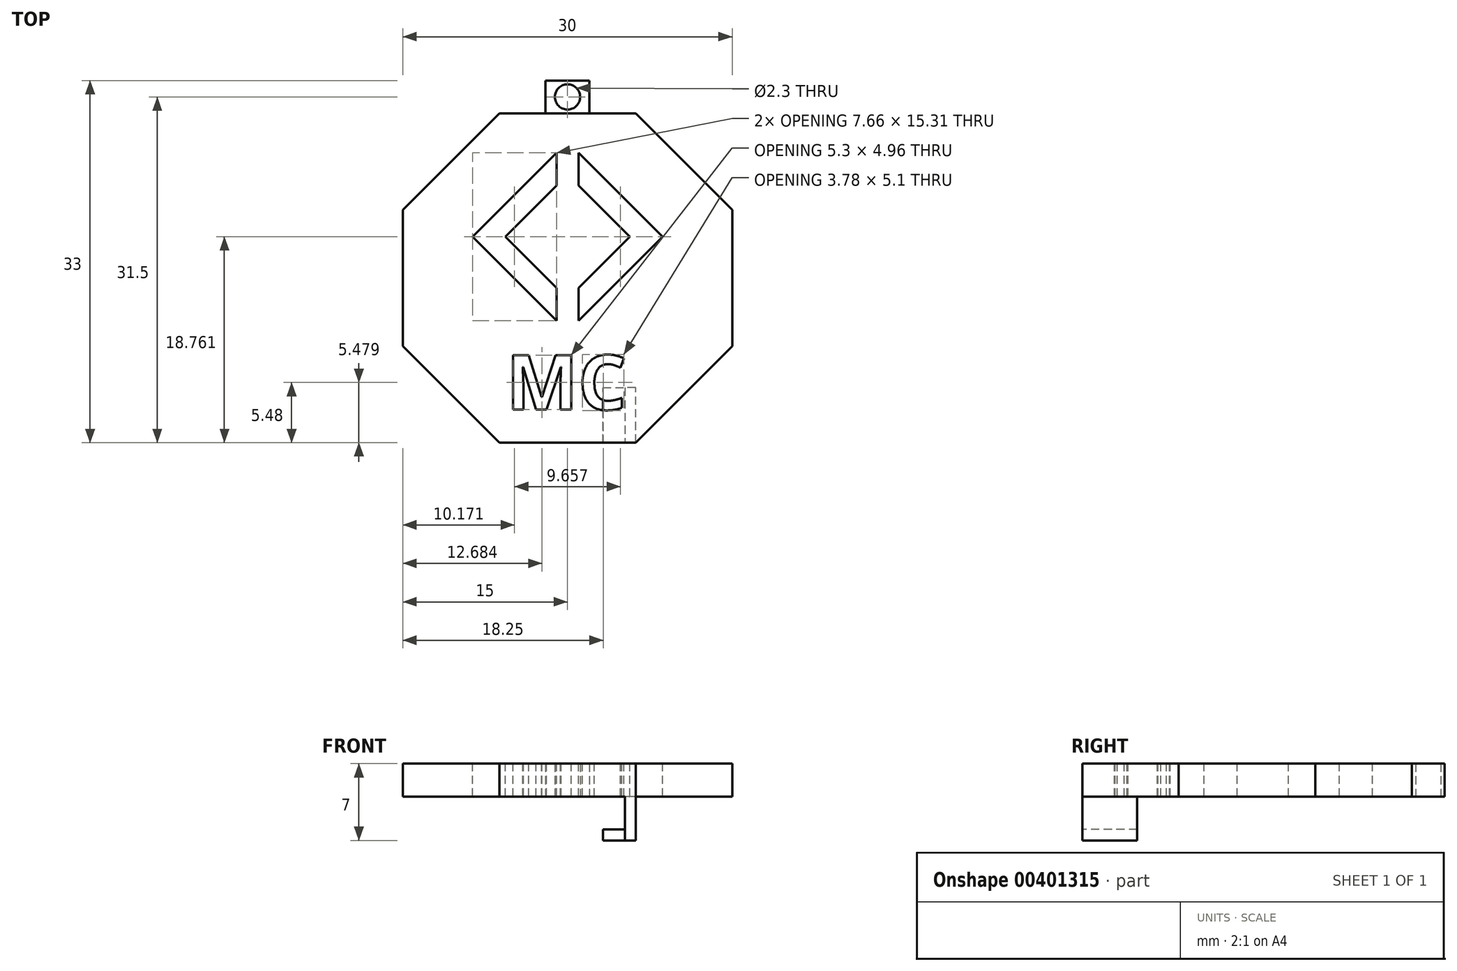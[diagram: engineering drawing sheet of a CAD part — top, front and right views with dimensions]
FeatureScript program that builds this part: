
annotation { "Feature Type Name" : "Feature", "Feature Type Description" : "" }
export const myFeature = defineFeature(function(context is Context, id is Id, definition is map)
    precondition{}
    {
        {
            var Q0;
            Q0=qCreatedBy(makeId("Top.planeOp"),FACE);
            var sketch = newSketch(context, id + "F0", { "sketchPlane" : qUnion([Q0])});
            skCircle(sketch, "E0.cCircle", {"center": v(0, 0) * mm, "radius": 15 * mm, "construction": true});
            skLineSegment(sketch, "E0.0", {"start": v(15, 6.21) * mm, "end": v(15, -6.21) * mm});
            skLineSegment(sketch, "E0.1", {"start": v(15, -6.21) * mm, "end": v(6.21, -15) * mm});
            skLineSegment(sketch, "E0.2", {"start": v(6.21, -15) * mm, "end": v(-6.21, -15) * mm});
            skLineSegment(sketch, "E0.3", {"start": v(-6.21, -15) * mm, "end": v(-15, -6.21) * mm});
            skLineSegment(sketch, "E0.4", {"start": v(-15, -6.21) * mm, "end": v(-15, 6.21) * mm});
            skLineSegment(sketch, "E0.5", {"start": v(-15, 6.21) * mm, "end": v(-6.21, 15) * mm});
            skLineSegment(sketch, "E0.6", {"start": v(-6.21, 15) * mm, "end": v(6.21, 15) * mm});
            skLineSegment(sketch, "E0.7", {"start": v(6.21, 15) * mm, "end": v(15, 6.21) * mm});
            skPoint(sketch, "E0.0.midPoint", {"position": v(15, 0) * mm});
            skLineSegment(sketch, "E1", {"start": v(0, 0) * mm, "end": v(-15, 0) * mm, "construction": true});
            skSolve(sketch);
        }
        {
            var Q0;
            Q0=qSketchRegion(id+"F0",true);
            extrude(context, id + "F1", {"entities" : qUnion([Q0]), "depth" : 3 * mm});
        }
        {
            var Q0;
            Q0=makeQuery(id+"F1.opExtrude","CAP_FACE",FACE,{"disambiguationData":[OSD([sQuery(id+"F0.wireOp",EDGE,"E0.0"),sQuery(id+"F0.wireOp",EDGE,"E0.1"),sQuery(id+"F0.wireOp",EDGE,"E0.2"),sQuery(id+"F0.wireOp",EDGE,"E0.3"),sQuery(id+"F0.wireOp",EDGE,"E0.4"),sQuery(id+"F0.wireOp",EDGE,"E0.5"),sQuery(id+"F0.wireOp",EDGE,"E0.6"),sQuery(id+"F0.wireOp",EDGE,"E0.7")])],"isStart":false});
            var sketch = newSketch(context, id + "F2", { "sketchPlane" : qUnion([Q0])});
            skText(sketch, "E2", { "text": "MC", "fontName": "OpenSans-Bold.ttf"});
            skArc(sketch, "E3.cCircle", {"start": v(2.83, 0.93) * mm, "mid": v(0, 7.76) * mm, "end": v(-2.83, 0.93) * mm, "construction": true});
            skLineSegment(sketch, "E3.0", {"start": v(5.66, 3.76) * mm, "end": v(1, -0.9) * mm});
            skLineSegment(sketch, "E3.2", {"start": v(-5.66, 3.76) * mm, "end": v(-1, 8.42) * mm});
            skLineSegment(sketch, "E3.3", {"start": v(1, 8.42) * mm, "end": v(5.66, 3.76) * mm});
            skPoint(sketch, "E3.0.midPoint", {"position": v(2.83, 0.93) * mm});
            skLineSegment(sketch, "E4", {"start": v(-5.66, 3.76) * mm, "end": v(0, 3.76) * mm, "construction": true});
            skLineSegment(sketch, "E5.1", {"start": v(8.66, 3.76) * mm, "end": v(1, -3.9) * mm});
            skLineSegment(sketch, "E5.3", {"start": v(-8.66, 3.76) * mm, "end": v(-1, 11.42) * mm});
            skPoint(sketch, "E5.0.midPoint", {"position": v(4.33, 8.1) * mm});
            skLineSegment(sketch, "E6", {"start": v(-8.66, 3.76) * mm, "end": v(-5.66, 3.76) * mm, "construction": true});
            skPoint(sketch, "E7.orphan", {"position": v(0, -1.9) * mm});
            skPoint(sketch, "E8.orphan", {"position": v(0, -4.9) * mm});
            skPoint(sketch, "E9.orphan", {"position": v(0.45, -660.17) * mm});
            skPoint(sketch, "E10.orphan", {"position": v(-0.45, -23.95) * mm});
            skLineSegment(sketch, "E11.trimOffspring", {"start": v(0, 3.76) * mm, "end": v(8.66, 3.76) * mm, "construction": true});
            skPoint(sketch, "E12.orphan", {"position": v(0, 9.42) * mm});
            skPoint(sketch, "E13.orphan", {"position": v(0, 12.42) * mm});
            skPoint(sketch, "E14.bottom.end.orphan", {"position": v(0.45, 31.48) * mm});
            skPoint(sketch, "E14.bottom.start.orphan", {"position": v(-0.45, 667.69) * mm});
            skPoint(sketch, "E15.firstSnap0", {"position": v(-10.6, -10.6) * mm});
            skPoint(sketch, "E15.secondSnap0", {"position": v(10.6, 10.6) * mm});
            skPoint(sketch, "E16.startSnap0", {"position": v(0.45, 11.37) * mm});
            skLineSegment(sketch, "E17", {"start": v(1, 11.42) * mm, "end": v(1, 8.42) * mm});
            skLineSegment(sketch, "E18", {"start": v(-1, 11.42) * mm, "end": v(-1, 8.42) * mm});
            skPoint(sketch, "E19.orphan", {"position": v(0.45, 12.87) * mm});
            skLineSegment(sketch, "E20.trimOffspring", {"start": v(1, 11.42) * mm, "end": v(8.66, 3.76) * mm});
            skPoint(sketch, "E21.trimOffspring.end.orphan", {"position": v(0.45, 9.87) * mm});
            skLineSegment(sketch, "E22.trimOffspring", {"start": v(-1, -0.9) * mm, "end": v(-5.66, 3.76) * mm});
            skLineSegment(sketch, "E23.trimOffspring", {"start": v(-1, -0.9) * mm, "end": v(-1, -3.9) * mm});
            skLineSegment(sketch, "E24.trimOffspring", {"start": v(1, -0.9) * mm, "end": v(1, -3.9) * mm});
            skLineSegment(sketch, "E25.trimOffspring", {"start": v(-1, -3.9) * mm, "end": v(-8.66, 3.76) * mm});
            const initialGuessF2  = {"E2": [-0.00559, -0.012, 1, 0, 0.005]};
            skSetInitialGuess(sketch, initialGuessF2);
            skSolve(sketch);
        }
        {
            var Q0;
            Q0=qSketchRegion(id+"F2",true);
            extrude(context, id + "F3", {"entities" : qUnion([Q0]), "operationType" : NewBodyOperationType.REMOVE, "endBound" : BoundingType.THROUGH_ALL, "oppositeDirection" : true, "depth" : 3 * mm});
        }
        {
            var Q0;
            Q0=makeQuery(id+"F1.opExtrude","CAP_FACE",FACE,{"disambiguationData":[OSD([sQuery(id+"F0.wireOp",EDGE,"E0.0"),sQuery(id+"F0.wireOp",EDGE,"E0.1"),sQuery(id+"F0.wireOp",EDGE,"E0.2"),sQuery(id+"F0.wireOp",EDGE,"E0.3"),sQuery(id+"F0.wireOp",EDGE,"E0.4"),sQuery(id+"F0.wireOp",EDGE,"E0.5"),sQuery(id+"F0.wireOp",EDGE,"E0.6"),sQuery(id+"F0.wireOp",EDGE,"E0.7")])],"isStart":true});
            var sketch = newSketch(context, id + "F4", { "sketchPlane" : qUnion([Q0])});
            skLineSegment(sketch, "E26.bottom", {"start": v(6.21, 15) * mm, "end": v(5.21, 15) * mm});
            skLineSegment(sketch, "E26.top", {"start": v(6.21, 10) * mm, "end": v(5.21, 10) * mm});
            skLineSegment(sketch, "E26.left", {"start": v(6.21, 15) * mm, "end": v(6.21, 10) * mm});
            skLineSegment(sketch, "E26.right", {"start": v(5.21, 15) * mm, "end": v(5.21, 10) * mm});
            skSolve(sketch);
        }
        {
            var Q0;
            Q0=qSketchRegion(id+"F4",true);
            extrude(context, id + "F5", {"entities" : qUnion([Q0]), "operationType" : NewBodyOperationType.ADD, "depth" : 4 * mm});
        }
        {
            var Q0;
            Q0=makeQuery(id+"F5.opExtrude","SWEPT_FACE",FACE,{"disambiguationData":[OSD([sQuery(id+"F4.wireOp",EDGE,"E26.right")])]});
            var sketch = newSketch(context, id + "F6", { "sketchPlane" : qUnion([Q0])});
            skLineSegment(sketch, "E27.bottom", {"start": v(10, -4) * mm, "end": v(15, -4) * mm});
            skLineSegment(sketch, "E27.top", {"start": v(10, -3) * mm, "end": v(15, -3) * mm});
            skLineSegment(sketch, "E27.left", {"start": v(10, -4) * mm, "end": v(10, -3) * mm});
            skLineSegment(sketch, "E27.right", {"start": v(15, -4) * mm, "end": v(15, -3) * mm});
            skSolve(sketch);
        }
        {
            var Q0;
            Q0=makeQuery(id+"F6.imprint","IMPRINT",FACE,{"disambiguationData":[TD([[makeQuery(id+"F6.imprint","IMPRINT",EDGE,{"derivedFrom":sQuery(id+"F6.wireOp",EDGE,"E27.bottom")}),-1.0]])]});
            var Q1;
            Q1=sQuery(id+"F6.wireOp",EDGE,"E27.top");
            var Q2;
            Q2=sQuery(id+"F6.wireOp",EDGE,"E27.bottom");
            var Q3;
            Q3=sQuery(id+"F6.wireOp",EDGE,"E27.right");
            var Q4;
            Q4=sQuery(id+"F6.wireOp",EDGE,"E27.left");
            extrude(context, id + "F7", {"entities" : qUnion([Q0]), "surfaceEntities" : qUnion([Q1, Q2, Q3, Q4]), "depth" : 2 * mm});
        }
        {
            var Q0;
            Q0=makeQuery(id+"F1.opExtrude","SWEPT_FACE",FACE,{"disambiguationData":[OSD([sQuery(id+"F0.wireOp",EDGE,"E0.6")])]});
            var sketch = newSketch(context, id + "F8", { "sketchPlane" : qUnion([Q0])});
            skLineSegment(sketch, "E28.bottom", {"start": v(2, 3) * mm, "end": v(-2, 3) * mm});
            skLineSegment(sketch, "E28.top", {"start": v(2, 0) * mm, "end": v(-2, 0) * mm});
            skLineSegment(sketch, "E28.left", {"start": v(2, 3) * mm, "end": v(2, 0) * mm});
            skLineSegment(sketch, "E28.right", {"start": v(-2, 3) * mm, "end": v(-2, 0) * mm});
            skPoint(sketch, "E28.middle", {"position": v(0, 1.5) * mm});
            skPoint(sketch, "E28.middle.positionSnap0", {"position": v(0, 3) * mm});
            skPoint(sketch, "E28.centerSnap0", {"position": v(0, 3) * mm});
            skSolve(sketch);
        }
        {
            var Q0;
            Q0=qSketchRegion(id+"F8",true);
            extrude(context, id + "F9", {"entities" : qUnion([Q0]), "depth" : 3 * mm});
        }
        {
            var Q0;
            Q0=makeQuery(id+"F9.opExtrude","SWEPT_FACE",FACE,{"disambiguationData":[OSD([sQuery(id+"F8.wireOp",EDGE,"E28.top")])]});
            var sketch = newSketch(context, id + "F10", { "sketchPlane" : qUnion([Q0])});
            skCircle(sketch, "E29", {"center": v(0, -16.5) * mm, "radius": 1.15 * mm});
            skLineSegment(sketch, "E30", {"start": v(0, -16.5) * mm, "end": v(0, -15) * mm, "construction": true});
            skLineSegment(sketch, "E31", {"start": v(0, -16.5) * mm, "end": v(0, -18) * mm, "construction": true});
            skSolve(sketch);
        }
        {
            var Q0;
            Q0=qSketchRegion(id+"F10",true);
            extrude(context, id + "F11", {"entities" : qUnion([Q0]), "operationType" : NewBodyOperationType.REMOVE, "endBound" : BoundingType.THROUGH_ALL, "oppositeDirection" : true, "depth" : 25 * mm});
        }
    });
